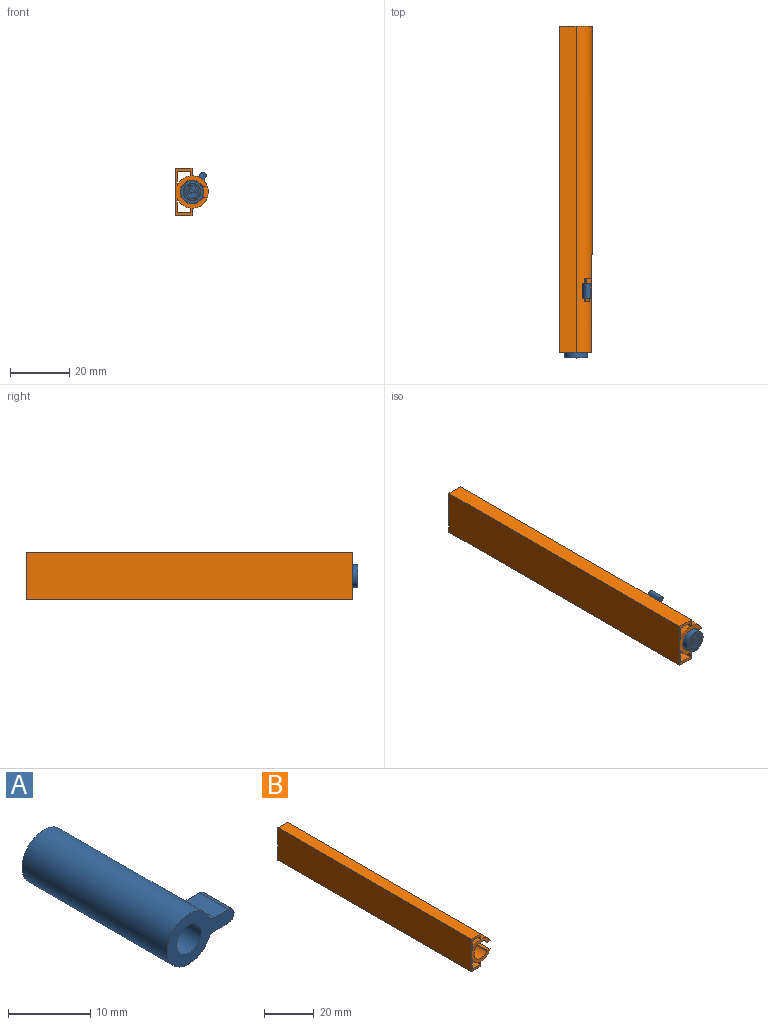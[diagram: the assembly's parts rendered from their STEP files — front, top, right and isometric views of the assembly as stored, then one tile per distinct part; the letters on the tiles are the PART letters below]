
ASSEMBLY  parts=2 mates=1
PART A: 38 faces, bbox 11.5x25x7.5 mm
  f0: plane 7.5x7.5mm, normal (0,1,0), area 15.9mm2, adj f1,f12
  f1: cylinder r=3.75mm len=25mm, axis (0,1,0), area 572.8mm2, adj f0,f2,f5,f6,f7
  f2: plane 11.5x7.5mm, normal (0,-1,0), area 38.1mm2, adj f1,f3,f4,f6,f7,f8,f9
  f3: plane 5x2.44mm, normal (0,0,1), area 12.2mm2, adj f2,f5,f6,f8
  f4: plane 5x2.44mm, normal (0,0,-1), area 12.2mm2, adj f2,f5,f7,f8
  f5: plane 4.35x3.16mm, normal (0,1,0), area 7.8mm2, adj f1,f3,f4,f6,f7,f8
  f6: cylinder r=1mm len=5mm, axis (0,1,0), area 5.7mm2, adj f1,f2,f3,f5
  f7: cylinder r=1mm len=5mm, axis (0,1,0), area 5.7mm2, adj f1,f2,f4,f5
  f8: cylinder r=1mm len=5mm, axis (0,1,0), area 15.7mm2, adj f2,f3,f4,f5
  f9: cylinder r=2.1mm len=14mm, axis (0,-1,0), area 184.7mm2, adj f2,f37
  f10: plane 2.2x2.2mm, normal (0,-1,0), area 3.8mm2, adj f37
  f11: cylinder r=2.75mm len=5.5mm, axis (0,1,0), area 17.3mm2, adj f13,f14
  f12: cylinder r=3mm len=6mm, axis (0,1,0), area 18.8mm2, adj f0,f13
  f13: plane 6x6mm, normal (0,1,0), area 4.5mm2, adj f11,f12
  f14: plane 5.5x5.5mm, normal (0,1,0), area 7.5mm2, adj f11,f15,f16,f17,f18,f19,f26
  f15: plane 2.17x1.25mm, normal (0.87,0,-0.5), area 2.5mm2, adj f14,f16,f26,f27
  f16: plane 2.5x1mm, normal (0,0,-1), area 2.5mm2, adj f14,f15,f17,f27
  f17: plane 2.17x1.25mm, normal (-0.87,0,-0.5), area 2.5mm2, adj f14,f16,f18,f27
  f18: plane 2.17x1.25mm, normal (-0.87,0,0.5), area 2.5mm2, adj f14,f17,f19,f27
  f19: plane 2.5x1mm, normal (0,0,1), area 2.5mm2, adj f14,f18,f26,f27
  f20: plane 2x1mm, normal (0,0,-1), area 2mm2, adj f21,f25,f27,f28
  f21: plane 1.73x1mm, normal (0.87,0,-0.5), area 2mm2, adj f20,f22,f27,f28
  f22: plane 1.73x1mm, normal (0.87,0,0.5), area 2mm2, adj f21,f23,f27,f28
  f23: plane 2x1mm, normal (0,0,1), area 2mm2, adj f22,f24,f27,f28
  f24: plane 1.73x1mm, normal (-0.87,0,0.5), area 2mm2, adj f23,f25,f27,f28
  f25: plane 1.73x1mm, normal (-0.87,0,-0.5), area 2mm2, adj f20,f24,f27,f28
  f26: plane 2.17x1.25mm, normal (0.87,0,0.5), area 2.5mm2, adj f14,f15,f19,f27
  f27: plane 5x4.33mm, normal (0,1,0), area 5.8mm2, adj f15,f16,f17,f18,f19,f20,f21,f22
  f28: plane 4x3.46mm, normal (0,1,0), area 7.5mm2, adj f20,f21,f22,f23,f24,f25,f29,f30
  f29: plane 2.85x1mm, normal (-1,0,0.02), area 2.9mm2, adj f28,f30,f34,f35
  f30: plane 1.98x1mm, normal (0.32,0,0.95), area 2.1mm2, adj f28,f29,f34,f35
  f31: plane 1.47x1mm, normal (-0.32,0,-0.95), area 1.6mm2, adj f32,f33,f35,f36
  f32: plane 2.24x1mm, normal (1,0,-0.04), area 2.2mm2, adj f31,f33,f35,f36
  f33: plane 1.75x1.57mm, normal (-0.74,0,0.67), area 2.3mm2, adj f31,f32,f35,f36
  f34: plane 2.18x2.03mm, normal (0.73,0,-0.68), area 3mm2, adj f28,f29,f30,f35
  f35: plane 2.85x2.03mm, normal (0,1,0), area 1.2mm2, adj f29,f30,f31,f32,f33,f34
  f36: plane 2.24x1.57mm, normal (0,1,0), area 1.7mm2, adj f31,f32,f33
  f37: torus R=1.1mm, axis (0,-1,0), area 17.1mm2, adj f9,f10
PART B: 44 faces, bbox 11x110x16 mm
  f0: plane 5.5x1.3mm, normal (0.87,0,0.5), area 8.2mm2, adj f2,f3,f4,f15
  f1: plane 2x1.3mm, normal (0.87,0,-0.5), area 3mm2, adj f2,f4,f29,f37
  f2: cylinder r=5.5mm len=110mm, axis (0,1,0), area 1712.5mm2, adj f0,f1,f3,f9,f11,f12,f13,f14
  f3: plane 3.12x2.76mm, normal (0,1,0), area 4.2mm2, adj f0,f2,f4,f13,f38,f39,f42
  f4: cylinder r=4mm len=95mm, axis (0,1,0), area 2204.4mm2, adj f0,f1,f3,f10,f12,f15,f16,f17
  f5: cylinder r=5.5mm len=110mm, axis (0,1,0), area 635.3mm2, adj f11,f12,f22,f27
  f6: cylinder r=5.5mm len=110mm, axis (0,1,0), area 635.3mm2, adj f11,f12,f26,f28
  f7: plane 110x4.5mm, normal (0,0,-1), area 495mm2, adj f11,f12,f22,f27
  f8: plane 110x4.5mm, normal (0,0,1), area 495mm2, adj f11,f12,f26,f28
  f9: plane 8x1.62mm, normal (0,0,-1), area 13mm2, adj f2,f15,f18,f43
  f10: cone r=4mm half-angle=9.5deg, axis (0,-1,0), area 262.8mm2, adj f4,f11
  f11: plane 16x11mm, normal (0,1,0), area 105.9mm2, adj f2,f5,f6,f7,f8,f10,f20,f21
  f12: plane 16x10.62mm, normal (0,-1,0), area 56.5mm2, adj f2,f4,f5,f6,f7,f8,f13,f14
  f13: plane 27.5x1.62mm, normal (0,0,1), area 44.6mm2, adj f2,f3,f12,f42
  f14: plane 19.5x1.62mm, normal (0,0,-1), area 31.7mm2, adj f2,f12,f17,f41
  f15: plane 6.97x3.5mm, normal (0,-1,0), area 10.6mm2, adj f0,f2,f4,f9,f43
  f16: plane 5.5x1.3mm, normal (0.87,0,-0.5), area 8.2mm2, adj f2,f4,f17,f18
  f17: plane 3.12x2.76mm, normal (0,1,0), area 4.2mm2, adj f2,f4,f14,f16,f35,f36,f41
  f18: plane 3.12x2.76mm, normal (0,-1,0), area 4.4mm2, adj f2,f4,f9,f16,f43
  f19: plane 2x1.3mm, normal (0.87,0,0.5), area 3mm2, adj f2,f4,f31,f40
  f20: plane 110x5.5mm, normal (0,0,1), area 605mm2, adj f11,f12,f21,f23
  f21: plane 110x16mm, normal (-1,0,0), area 1760mm2, adj f11,f12,f20,f24
  f22: plane 110x1.52mm, normal (-1,0,0), area 167.5mm2, adj f5,f7,f11,f12
  f23: plane 110x2.5mm, normal (1,0,0), area 275mm2, adj f2,f11,f12,f20
  f24: plane 110x5.5mm, normal (0,0,-1), area 605mm2, adj f11,f12,f21,f25
  f25: plane 110x2.5mm, normal (1,0,0), area 275mm2, adj f2,f11,f12,f24
  f26: plane 110x1.52mm, normal (-1,0,0), area 167.5mm2, adj f6,f8,f11,f12
  f27: plane 110x4.71mm, normal (1,0,0), area 518mm2, adj f5,f7,f11,f12
  f28: plane 110x4.71mm, normal (1,0,0), area 518mm2, adj f6,f8,f11,f12
  f29: plane 1.94x1.78mm, normal (0,1,0), area 1.8mm2, adj f1,f2,f4,f34
  f30: plane 1.25x1mm, normal (-0.56,0,0.83), area 1.5mm2, adj f2,f4,f34,f37
  f31: plane 1.94x1.78mm, normal (0,1,0), area 1.8mm2, adj f2,f4,f19,f33
  f32: plane 1.25x1mm, normal (-0.56,0,-0.83), area 1.5mm2, adj f2,f4,f33,f40
  f33: cylinder r=1mm len=1.91mm, axis (-0.83,0,0.56), area 2.4mm2, adj f2,f4,f31,f32
  f34: cylinder r=1mm len=1.91mm, axis (0.83,0,0.56), area 2.4mm2, adj f2,f4,f29,f30
  f35: plane 1.33x1.24mm, normal (-0.68,0,-0.73), area 0.9mm2, adj f4,f17,f37
  f36: plane 1.82x1.71mm, normal (0.68,0,0.73), area 1.2mm2, adj f2,f17,f37
  f37: plane 2.57x2.54mm, normal (0,-1,0), area 3.2mm2, adj f1,f30,f35,f36
  f38: plane 1.33x1.24mm, normal (-0.68,0,0.73), area 0.9mm2, adj f3,f4,f40
  f39: plane 1.82x1.71mm, normal (0.68,0,-0.73), area 1.2mm2, adj f2,f3,f40
  f40: plane 2.57x2.54mm, normal (0,-1,0), area 3.2mm2, adj f19,f32,f38,f39
  f41: cylinder r=1.5mm len=19.5mm, axis (0,-1,0), area 5.1mm2, adj f4,f12,f14,f17
  f42: cylinder r=1.5mm len=27.5mm, axis (0,-1,0), area 7.2mm2, adj f3,f4,f12,f13
  f43: cylinder r=1.5mm len=8mm, axis (0,-1,0), area 2.1mm2, adj f4,f9,f15,f18
PLACE A rot(axis=(0.88,0,0.47),180deg) t=(-18.7,-74.27,-7.09)mm
PLACE B t=(-18.7,37.65,-7.09)mm fixed
MATE cylindrical A.f1 <-> B.f2  axis (0,1,0) through (-18.7,-49.27,-7.09)mm
